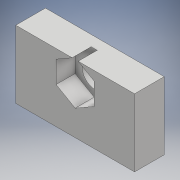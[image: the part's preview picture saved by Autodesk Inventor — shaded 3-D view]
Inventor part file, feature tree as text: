
AUTODESK INVENTOR PART (.ipt)
format: ipt  version: 2017 (Build 210142000, 142)  size: 121,856 bytes
history: native  units: mm
features: extrude x3, sketch x3, projected_geometry x1
ambient origin geometry x8: Origin, YZ Plane, XZ Plane, XY Plane, X Axis, Y Axis, Z Axis, Center Point
bodies: Solid1 (feature_tree)
feature tree (7):
  extrude  "Extrusion1"  Depth=25.0mm
  extrude  "Extrusion2"  Depth=6.25mm TaperAngle=0.0deg
  extrude  "Extrusion3"  Depth=2.25mm TaperAngle=0.0deg
  sketch  "Sketch1"  dims[d0=25.0mm d1=20.0mm]
  sketch  "Sketch2"  dims[d2=8.0mm d3=6.25mm d4=0.0mm]
  sketch  "Sketch3"  dims[d5=5.5mm d6=2.25mm d7=0.0mm d8=5.75mm d9=0.0mm]
  projected_geometry  "Projected Loop1"
